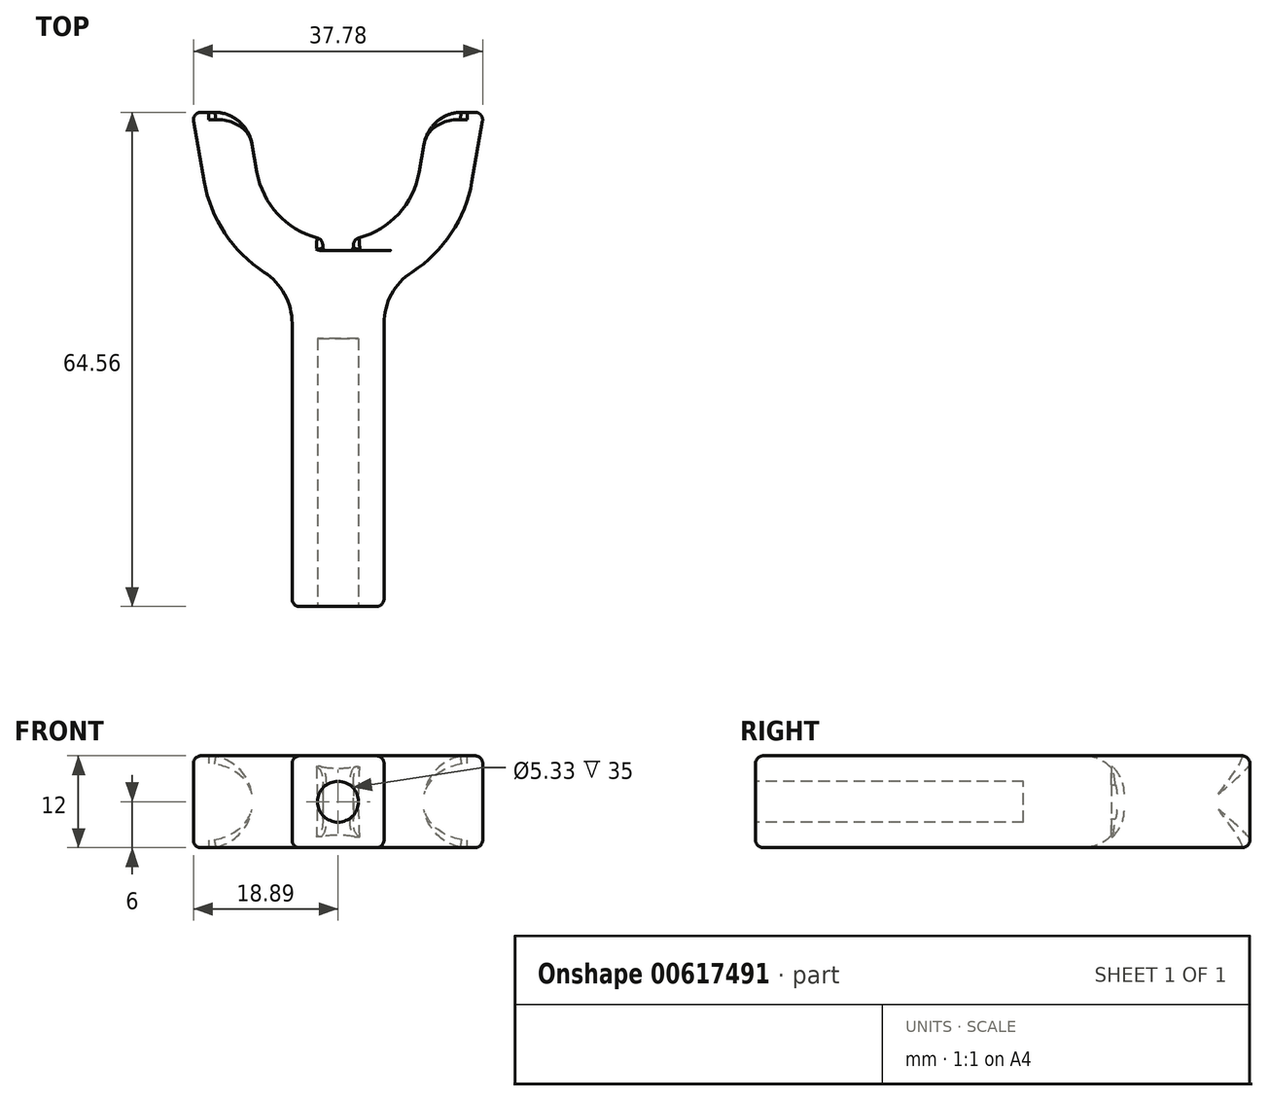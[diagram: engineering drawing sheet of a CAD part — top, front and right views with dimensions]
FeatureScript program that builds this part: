
annotation { "Feature Type Name" : "Feature", "Feature Type Description" : "" }
export const myFeature = defineFeature(function(context is Context, id is Id, definition is map)
    precondition{}
    {
        {
            var Q0;
            Q0=qCreatedBy(makeId("Top.planeOp"),FACE);
            var sketch = newSketch(context, id + "F0", { "sketchPlane" : qUnion([Q0])});
            skLineSegment(sketch, "E0.right", {"start": v(6, -16.7) * mm, "end": v(6, -58.56) * mm});
            skLineSegment(sketch, "E1", {"start": v(0, -58.56) * mm, "end": v(0, 0) * mm, "construction": true});
            skArc(sketch, "E2", {"start": v(2, -10.56) * mm, "mid": v(7.65, -7.55) * mm, "end": v(10.59, -1.87) * mm});
            skArc(sketch, "E3", {"start": v(6, -16.7) * mm, "mid": v(13.57, -11.44) * mm, "end": v(17.48, -3.08) * mm});
            skLineSegment(sketch, "E4", {"start": v(10.59, -1.87) * mm, "end": v(17.48, -3.08) * mm, "construction": true});
            skLineSegment(sketch, "E5", {"start": v(6, -58.56) * mm, "end": v(0, -58.56) * mm});
            skLineSegment(sketch, "E6", {"start": v(10.59, -1.87) * mm, "end": v(11.97, 6) * mm});
            skLineSegment(sketch, "E7", {"start": v(11.97, 6) * mm, "end": v(19.08, 6) * mm});
            skLineSegment(sketch, "E8", {"start": v(19.08, 6) * mm, "end": v(17.48, -3.08) * mm});
            skLineSegment(sketch, "E9", {"start": v(2, -10.56) * mm, "end": v(2, -12.06) * mm});
            skLineSegment(sketch, "E10", {"start": v(2, -12.06) * mm, "end": v(0, -12.06) * mm});
            skLineSegment(sketch, "E11", {"start": v(0, -12.06) * mm, "end": v(0, -58.56) * mm});
            skArc(sketch, "E12.MirrorCS", {"start": v(-2, -10.56) * mm, "mid": v(-7.65, -7.55) * mm, "end": v(-10.59, -1.87) * mm});
            skLineSegment(sketch, "E13.MirrorCS", {"start": v(-2, -12.06) * mm, "end": v(0, -12.06) * mm});
            skLineSegment(sketch, "E14.MirrorCS", {"start": v(-2, -10.56) * mm, "end": v(-2, -12.06) * mm});
            skLineSegment(sketch, "E15.MirrorCS", {"start": v(-10.59, -1.87) * mm, "end": v(-17.48, -3.08) * mm, "construction": true});
            skLineSegment(sketch, "E16.MirrorCS", {"start": v(-10.59, -1.87) * mm, "end": v(-11.97, 6) * mm});
            skLineSegment(sketch, "E17.MirrorCS", {"start": v(-11.97, 6) * mm, "end": v(-19.08, 6) * mm});
            skLineSegment(sketch, "E18.MirrorCS", {"start": v(-19.08, 6) * mm, "end": v(-17.48, -3.08) * mm});
            skArc(sketch, "E19.MirrorCS", {"start": v(-6, -16.7) * mm, "mid": v(-13.57, -11.44) * mm, "end": v(-17.48, -3.08) * mm});
            skLineSegment(sketch, "E20.MirrorCS", {"start": v(-6, -16.7) * mm, "end": v(-6, -58.56) * mm});
            skLineSegment(sketch, "E21.MirrorCS", {"start": v(-6, -58.56) * mm, "end": v(0, -58.56) * mm});
            skSolve(sketch);
        }
        {
            var Q0;
            Q0 = qSketchRegion(id + "F0", true);
            extrude(context, id + "F1", {"entities" : qUnion([Q0]), "depth" : 12 * mm, "offsetDistance" : 25 * mm});
        }
        {
            var Q0;
            Q0=makeQuery(id+"F1.opExtrude","SWEPT_FACE",FACE,{"disambiguationData":[OSD([sQuery(id+"F0.wireOp",EDGE,"E5"),sQuery(id+"F0.wireOp",EDGE,"E21.MirrorCS")])]});
            var sketch = newSketch(context, id + "F2", { "sketchPlane" : qUnion([Q0])});
            skPoint(sketch, "E22", {"position": v(0, 6) * mm});
            skCircle(sketch, "E23", {"center": v(0, 6) * mm, "radius": 2.67 * mm});
            skSolve(sketch);
        }
        {
            var Q0;
            Q0 = qSketchRegion(id + "F2", true);
            extrude(context, id + "F3", {"entities" : qUnion([Q0]), "operationType" : NewBodyOperationType.REMOVE, "oppositeDirection" : true, "depth" : 35 * mm, "offsetDistance" : 25 * mm});
        }
        {
            var Q0;
            Q0=makeQuery(id+"F1.opExtrude","SWEPT_EDGE",EDGE,{"disambiguationData":[OSD([sQuery(id+"F0.wireOp",EDGE,"E6"),sQuery(id+"F0.wireOp",EDGE,"E7")])]});
            var Q1;
            Q1=makeQuery(id+"F1.opExtrude","CAP_EDGE",EDGE,{"disambiguationData":[OSD([sQuery(id+"F0.wireOp",EDGE,"E12.MirrorCS")])],"isStart":false});
            var Q2;
            Q2=makeQuery(id+"F1.opExtrude","CAP_EDGE",EDGE,{"disambiguationData":[OSD([sQuery(id+"F0.wireOp",EDGE,"E12.MirrorCS")])],"isStart":true});
            var Q3;
            Q3=makeQuery(id+"F1.opExtrude","SWEPT_EDGE",EDGE,{"disambiguationData":[OSD([sQuery(id+"F0.wireOp",EDGE,"E16.MirrorCS"),sQuery(id+"F0.wireOp",EDGE,"E17.MirrorCS")])]});
            var Q4;
            Q4=makeQuery(id+"F1.opExtrude","CAP_EDGE",EDGE,{"disambiguationData":[OSD([sQuery(id+"F0.wireOp",EDGE,"E2")])],"isStart":false});
            var Q5;
            Q5=makeQuery(id+"F1.opExtrude","CAP_EDGE",EDGE,{"disambiguationData":[OSD([sQuery(id+"F0.wireOp",EDGE,"E2")])],"isStart":true});
            fillet(context, id + "F4", {"entities" : qUnion([Q0, Q1, Q2, Q3, Q4, Q5]), "radius" : 5 * mm, "tangentPropagation" : true, "allowEdgeOverflow" : false});
        }
        {
            var Q0;
            Q0=makeQuery(id+"F1.opExtrude","SWEPT_EDGE",EDGE,{"disambiguationData":[OSD([sQuery(id+"F0.wireOp",EDGE,"E0.right"),sQuery(id+"F0.wireOp",EDGE,"E3")])]});
            var Q1;
            Q1=makeQuery(id+"F1.opExtrude","SWEPT_EDGE",EDGE,{"disambiguationData":[OSD([sQuery(id+"F0.wireOp",EDGE,"E19.MirrorCS"),sQuery(id+"F0.wireOp",EDGE,"E20.MirrorCS")])]});
            fillet(context, id + "F5", {"entities" : qUnion([Q0, Q1]), "radius" : 8 * mm, "tangentPropagation" : true, "allowEdgeOverflow" : false});
        }
        {
            var Q0;
            Q0=makeQuery(id+"F1.opExtrude","CAP_EDGE",EDGE,{"disambiguationData":[OSD([sQuery(id+"F0.wireOp",EDGE,"E0.right")])],"isStart":false});
            var Q1;
            Q1=makeQuery(id+"F1.opExtrude","CAP_EDGE",EDGE,{"disambiguationData":[OSD([sQuery(id+"F0.wireOp",EDGE,"E3")])],"isStart":false});
            var Q2;
            Q2=makeQuery(id+"F1.opExtrude","CAP_EDGE",EDGE,{"disambiguationData":[OSD([sQuery(id+"F0.wireOp",EDGE,"E9")])],"isStart":false});
            var Q3;
            Q3=makeQuery(id+"F1.opExtrude","CAP_EDGE",EDGE,{"disambiguationData":[OSD([sQuery(id+"F0.wireOp",EDGE,"E10"),sQuery(id+"F0.wireOp",EDGE,"E13.MirrorCS")])],"isStart":false});
            var Q4;
            Q4=makeQuery(id+"F1.opExtrude","CAP_EDGE",EDGE,{"disambiguationData":[OSD([sQuery(id+"F0.wireOp",EDGE,"E14.MirrorCS")])],"isStart":false});
            var Q5;
            Q5=makeQuery(id+"F1.opExtrude","SWEPT_EDGE",EDGE,{"disambiguationData":[OSD([sQuery(id+"F0.wireOp",EDGE,"E12.MirrorCS"),sQuery(id+"F0.wireOp",EDGE,"E14.MirrorCS")])]});
            var Q6;
            Q6=makeQuery(id+"F1.opExtrude","SWEPT_EDGE",EDGE,{"disambiguationData":[OSD([sQuery(id+"F0.wireOp",EDGE,"E2"),sQuery(id+"F0.wireOp",EDGE,"E9")])]});
            var Q7;
            Q7=makeQuery(id+"F1.opExtrude","CAP_EDGE",EDGE,{"disambiguationData":[OSD([sQuery(id+"F0.wireOp",EDGE,"E7")])],"isStart":false});
            var Q8;
            Q8=makeQuery(id+"F1.opExtrude","SWEPT_EDGE",EDGE,{"disambiguationData":[OSD([sQuery(id+"F0.wireOp",EDGE,"E7"),sQuery(id+"F0.wireOp",EDGE,"E8")])]});
            var Q9;
            Q9=makeQuery(id+"F1.opExtrude","CAP_EDGE",EDGE,{"disambiguationData":[OSD([sQuery(id+"F0.wireOp",EDGE,"E7")])],"isStart":true});
            var Q10;
            Q10=makeQuery(id+"F1.opExtrude","CAP_EDGE",EDGE,{"disambiguationData":[OSD([sQuery(id+"F0.wireOp",EDGE,"E3")])],"isStart":true});
            var Q11;
            Q11=makeQuery(id+"F1.opExtrude","CAP_EDGE",EDGE,{"disambiguationData":[OSD([sQuery(id+"F0.wireOp",EDGE,"E0.right")])],"isStart":true});
            var Q12;
            Q12=makeQuery(id+"F1.opExtrude","CAP_EDGE",EDGE,{"disambiguationData":[OSD([sQuery(id+"F0.wireOp",EDGE,"E5"),sQuery(id+"F0.wireOp",EDGE,"E21.MirrorCS")])],"isStart":true});
            var Q13;
            Q13=makeQuery(id+"F1.opExtrude","SWEPT_EDGE",EDGE,{"disambiguationData":[OSD([sQuery(id+"F0.wireOp",EDGE,"E20.MirrorCS"),sQuery(id+"F0.wireOp",EDGE,"E21.MirrorCS")])]});
            var Q14;
            Q14=makeQuery(id+"F1.opExtrude","CAP_EDGE",EDGE,{"disambiguationData":[OSD([sQuery(id+"F0.wireOp",EDGE,"E5"),sQuery(id+"F0.wireOp",EDGE,"E21.MirrorCS")])],"isStart":false});
            var Q15;
            Q15=makeQuery(id+"F1.opExtrude","CAP_EDGE",EDGE,{"disambiguationData":[OSD([sQuery(id+"F0.wireOp",EDGE,"E20.MirrorCS")])],"isStart":false});
            var Q16;
            Q16=makeQuery(id+"F1.opExtrude","CAP_EDGE",EDGE,{"disambiguationData":[OSD([sQuery(id+"F0.wireOp",EDGE,"E20.MirrorCS")])],"isStart":true});
            var Q17;
            Q17=makeQuery(id+"F1.opExtrude","CAP_EDGE",EDGE,{"disambiguationData":[OSD([sQuery(id+"F0.wireOp",EDGE,"E19.MirrorCS")])],"isStart":false});
            var Q18;
            Q18=makeQuery(id+"F1.opExtrude","CAP_EDGE",EDGE,{"disambiguationData":[OSD([sQuery(id+"F0.wireOp",EDGE,"E19.MirrorCS")])],"isStart":true});
            var Q19;
            Q19=makeQuery(id+"F1.opExtrude","SWEPT_EDGE",EDGE,{"disambiguationData":[OSD([sQuery(id+"F0.wireOp",EDGE,"E17.MirrorCS"),sQuery(id+"F0.wireOp",EDGE,"E18.MirrorCS")])]});
            var Q20;
            Q20=makeQuery(id+"F1.opExtrude","CAP_EDGE",EDGE,{"disambiguationData":[OSD([sQuery(id+"F0.wireOp",EDGE,"E17.MirrorCS")])],"isStart":true});
            var Q21;
            Q21=makeQuery(id+"F1.opExtrude","CAP_EDGE",EDGE,{"disambiguationData":[OSD([sQuery(id+"F0.wireOp",EDGE,"E17.MirrorCS")])],"isStart":false});
            var Q22;
            Q22=makeQuery(id+"F1.opExtrude","CAP_EDGE",EDGE,{"disambiguationData":[OSD([sQuery(id+"F0.wireOp",EDGE,"E10"),sQuery(id+"F0.wireOp",EDGE,"E13.MirrorCS")])],"isStart":true});
            var Q23;
            Q23=makeQuery(id+"F1.opExtrude","CAP_EDGE",EDGE,{"disambiguationData":[OSD([sQuery(id+"F0.wireOp",EDGE,"E9")])],"isStart":true});
            var Q24;
            Q24=makeQuery(id+"F1.opExtrude","CAP_EDGE",EDGE,{"disambiguationData":[OSD([sQuery(id+"F0.wireOp",EDGE,"E14.MirrorCS")])],"isStart":true});
            var Q25;
            Q25=makeQuery(id+"F1.opExtrude","SWEPT_EDGE",EDGE,{"disambiguationData":[OSD([sQuery(id+"F0.wireOp",EDGE,"E0.right"),sQuery(id+"F0.wireOp",EDGE,"E5")])]});
            fillet(context, id + "F6", {"entities" : qUnion([Q0, Q1, Q2, Q3, Q4, Q5, Q6, Q7, Q8, Q9, Q10, Q11, Q12, Q13, Q14, Q15, Q16, Q17, Q18, Q19, Q20, Q21, Q22, Q23, Q24, Q25]), "radius" : 1 * mm, "tangentPropagation" : true, "allowEdgeOverflow" : false});
        }
        {
            var Q0;
            Q0=makeQuery(id+"F1.opExtrude","SWEPT_EDGE",EDGE,{"disambiguationData":[OSD([sQuery(id+"F0.wireOp",EDGE,"E9"),sQuery(id+"F0.wireOp",EDGE,"E10")])]});
            var Q1;
            Q1=makeQuery(id+"F1.opExtrude","SWEPT_EDGE",EDGE,{"disambiguationData":[OSD([sQuery(id+"F0.wireOp",EDGE,"E13.MirrorCS"),sQuery(id+"F0.wireOp",EDGE,"E14.MirrorCS")])]});
            var Q2;
            Q2=makeQuery(id+"F3.boolean.opBoolean","COPY",EDGE,{"derivedFrom":makeQuery(id+"F3.opExtrude","CAP_EDGE",EDGE,{"disambiguationData":[OSD([sQuery(id+"F2.wireOp",EDGE,"E23")])],"isStart":true})});
            fillet(context, id + "F7", {"entities" : qUnion([Q0, Q1, Q2]), "radius" : .5 * mm, "tangentPropagation" : true, "allowEdgeOverflow" : false});
        }
    });
